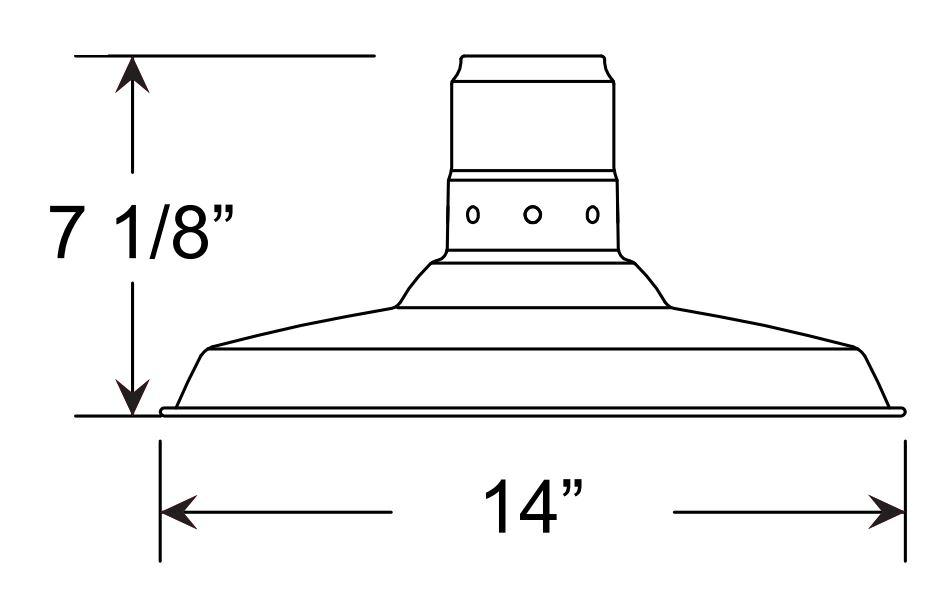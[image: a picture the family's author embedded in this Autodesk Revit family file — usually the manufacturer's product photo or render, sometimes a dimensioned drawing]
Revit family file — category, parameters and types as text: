
# Revit family: Urban Warehouse WFU5 14,16,18,20,22
name_source: partatom
category: Lighting Fixtures
units: mm (PartAtom-declared; Revit-internal decimal feet)

## family parameters
Always vertical = Yes
Cut with Voids When Loaded = No
Light Source = Yes
OmniClass Number = 23.80.70.00
OmniClass Title = Lighting
Part Type = Normal
Room Calculation Point = No
Round Connector Dimension = Use Diameter
Shared = No
Work Plane-Based = No

## types (5) — shared parameters
Apparent Load = 200 VA
BULB = Yes
Body Colour = Spun aluminium
Body Material = body
CRI = >90
Canopy Body = Aqua Green
Color Filter = 16777215
Construction Material = Heavy Duty spun aluminum.
Default Elevation = 0' - 0"
Description = 120-277 Voltage
Dimming = 1%
Dimming Lamp Color Temperature Shift = <None>
Efficiency = 65-125 lumens per watt
HUB = Putty
Lamp = Incandescent
Life = L70 50,000 hours
Load Classification = Lighting
Manufacturer = ANP Lighting
Photometric Web File = generic
Power Factor = 1
Tilt Angle = 90.00°
URL = https://www.anplighting.com
Voltage = 120 V
Warranty = 5 year limited warranty
Wattage Comments = 200 W Max
b = 0' - 3"

## per-type parameters (varying)
| type | Fixture Diameter | Fixture Height | WFU514 | WFU516 | WFU518 | WFU520 | WFU522 | Weight | a |
| WFU514 | 1' - 2" | 0' - 6 3/4" | Yes | No | No | No | No | 3.7 lb | 0' - 8" |
| WFU516 | 1' - 4" | 0' - 7 1/4" | No | Yes | No | No | No | 4.2 lb | 0' - 8 1/2" |
| WFU518 | 1' - 6" | 0' - 8" | No | No | Yes | No | No | 4.7 lb | 0' - 9" |
| WFU520 | 1' - 8" | 0' - 8 1/2" | No | No | No | Yes | No | 5.2 lb | 0' - 10" |
| WFU522 | 1' - 10" | 0' - 9 1/4" | No | No | No | No | Yes | 5.7 lb | 0' - 10" |

note: column(s) folded — value = type name in every type: Model

## geometry (parser evidence)
native form markers: Sweep x35
no freeform markers — native parametric forms only
